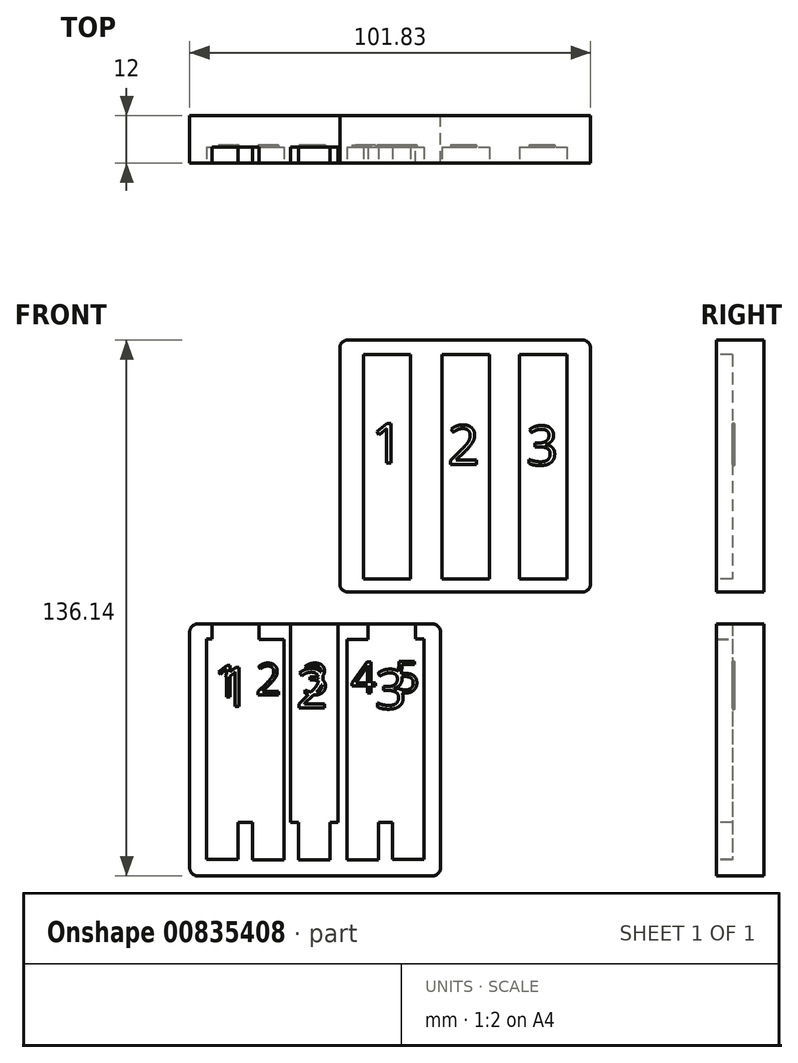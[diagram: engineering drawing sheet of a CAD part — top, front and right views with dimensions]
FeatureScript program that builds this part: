
annotation { "Feature Type Name" : "Feature", "Feature Type Description" : "" }
export const myFeature = defineFeature(function(context is Context, id is Id, definition is map)
    precondition{}
    {
        {
            var Q0;
            Q0=qCreatedBy(makeId("Front.planeOp"),FACE);
            var sketch = newSketch(context, id + "F0", { "sketchPlane" : qUnion([Q0])});
            skLineSegment(sketch, "E0.bottom", {"start": v(-35.21, 33.45) * mm, "end": v(28.49, 33.45) * mm});
            skLineSegment(sketch, "E0.top", {"start": v(-35.21, -30.55) * mm, "end": v(28.49, -30.55) * mm});
            skLineSegment(sketch, "E0.left", {"start": v(-35.21, 33.45) * mm, "end": v(-35.21, -30.55) * mm});
            skLineSegment(sketch, "E0.right", {"start": v(28.49, 33.45) * mm, "end": v(28.49, -30.55) * mm});
            skSolve(sketch);
        }
        {
            var Q0;
            Q0 = qSketchRegion(id + "F0", true);
            extrude(context, id + "F1", {"entities" : qUnion([Q0]), "depth" : 12 * mm, "offsetDistance" : 25 * mm});
        }
        {
            var Q0;
            Q0=makeQuery(id+"F1.opExtrude","CAP_FACE",FACE,{"disambiguationData":[OSD([sQuery(id+"F0.wireOp",EDGE,"E0.bottom"),sQuery(id+"F0.wireOp",EDGE,"E0.top"),sQuery(id+"F0.wireOp",EDGE,"E0.left"),sQuery(id+"F0.wireOp",EDGE,"E0.right")])],"isStart":false});
            var sketch = newSketch(context, id + "F2", { "sketchPlane" : qUnion([Q0])});
            skLineSegment(sketch, "E1.bottom", {"start": v(-30.9, 29.6) * mm, "end": v(-22.9, 29.6) * mm});
            skLineSegment(sketch, "E1.top", {"start": v(-30.9, -26.4) * mm, "end": v(-22.9, -26.4) * mm});
            skLineSegment(sketch, "E1.left", {"start": v(-30.9, 29.6) * mm, "end": v(-30.9, -26.4) * mm});
            skLineSegment(sketch, "E1.right", {"start": v(-22.9, 29.6) * mm, "end": v(-22.9, -26.4) * mm});
            skLineSegment(sketch, "E2.bottom", {"start": v(-19.28, 29.54) * mm, "end": v(-11.28, 29.54) * mm});
            skLineSegment(sketch, "E2.top", {"start": v(-19.28, -26.46) * mm, "end": v(-11.28, -26.46) * mm});
            skLineSegment(sketch, "E2.left", {"start": v(-19.28, 29.54) * mm, "end": v(-19.28, -26.46) * mm});
            skLineSegment(sketch, "E2.right", {"start": v(-11.28, 29.54) * mm, "end": v(-11.28, -26.46) * mm});
            skLineSegment(sketch, "E3.bottom", {"start": v(-7.55, 29.54) * mm, "end": v(0.45, 29.54) * mm});
            skLineSegment(sketch, "E3.top", {"start": v(-7.55, -26.46) * mm, "end": v(0.45, -26.46) * mm});
            skLineSegment(sketch, "E3.left", {"start": v(-7.55, 29.54) * mm, "end": v(-7.55, -26.46) * mm});
            skLineSegment(sketch, "E3.right", {"start": v(0.45, 29.54) * mm, "end": v(0.45, -26.46) * mm});
            skLineSegment(sketch, "E4.bottom", {"start": v(4.75, 29.54) * mm, "end": v(12.75, 29.54) * mm});
            skLineSegment(sketch, "E4.top", {"start": v(4.75, -26.46) * mm, "end": v(12.75, -26.46) * mm});
            skLineSegment(sketch, "E4.left", {"start": v(4.75, 29.54) * mm, "end": v(4.75, -26.46) * mm});
            skLineSegment(sketch, "E4.right", {"start": v(12.75, 29.54) * mm, "end": v(12.75, -26.46) * mm});
            skLineSegment(sketch, "E5.bottom", {"start": v(16.3, 29.59) * mm, "end": v(24.3, 29.59) * mm});
            skLineSegment(sketch, "E5.top", {"start": v(16.3, -26.41) * mm, "end": v(24.3, -26.41) * mm});
            skLineSegment(sketch, "E5.left", {"start": v(16.3, 29.59) * mm, "end": v(16.3, -26.41) * mm});
            skLineSegment(sketch, "E5.right", {"start": v(24.3, 29.59) * mm, "end": v(24.3, -26.41) * mm});
            skSolve(sketch);
        }
        {
            var Q0;
            Q0 = qSketchRegion(id + "F2", true);
            extrude(context, id + "F3", {"entities" : qUnion([Q0]), "operationType" : NewBodyOperationType.REMOVE, "oppositeDirection" : true, "depth" : 4 * mm, "offsetDistance" : 25 * mm});
        }
        {
            var Q0;
            Q0=makeQuery(id+"F3.boolean.opBoolean","COPY",FACE,{"derivedFrom":makeQuery(id+"F3.opExtrude","CAP_FACE",FACE,{"disambiguationData":[OSD([sQuery(id+"F2.wireOp",EDGE,"E1.bottom"),sQuery(id+"F2.wireOp",EDGE,"E1.top"),sQuery(id+"F2.wireOp",EDGE,"E1.left"),sQuery(id+"F2.wireOp",EDGE,"E1.right")])],"isStart":false})});
            var sketch = newSketch(context, id + "F4", { "sketchPlane" : qUnion([Q0])});
            skText(sketch, "E6", { "text": "1", "fontName": "OpenSans-Regular.ttf"});
            skText(sketch, "E7", { "text": "2", "fontName": "OpenSans-Regular.ttf"});
            skText(sketch, "E8", { "text": "3", "fontName": "OpenSans-Regular.ttf"});
            skText(sketch, "E9", { "text": "4", "fontName": "OpenSans-Regular.ttf"});
            skText(sketch, "E10", { "text": "5", "fontName": "OpenSans-Regular.ttf"});
            const initialGuessF4  = {"E6": [-0.0289, 0.01496, 1, 0, 0.008], "E7": [-0.01839, 0.01547, 1, 0, 0.008], "E8": [-0.00642, 0.01547, 1, 0, 0.008], "E9": [0.00585, 0.01587, 1, 0, 0.008], "E10": [0.01678, 0.01602, 1, 0, 0.008]};
            skSetInitialGuess(sketch, initialGuessF4);
            skSolve(sketch);
        }
        {
            var Q0;
            Q0 = qSketchRegion(id + "F4", true);
            extrude(context, id + "F5", {"entities" : qUnion([Q0]), "operationType" : NewBodyOperationType.REMOVE, "oppositeDirection" : true, "depth" : 0.5 * mm, "offsetDistance" : 25 * mm});
        }
        {
            var Q0;
            Q0=qCreatedBy(makeId("Front.planeOp"),FACE);
            var sketch = newSketch(context, id + "F6", { "sketchPlane" : qUnion([Q0])});
            skLineSegment(sketch, "E11.bottom", {"start": v(-35.58, 43.69) * mm, "end": v(28.12, 43.69) * mm});
            skLineSegment(sketch, "E11.top", {"start": v(-35.58, -20.31) * mm, "end": v(28.12, -20.31) * mm});
            skLineSegment(sketch, "E11.left", {"start": v(-35.58, 43.69) * mm, "end": v(-35.58, -20.31) * mm});
            skLineSegment(sketch, "E11.right", {"start": v(28.12, 43.69) * mm, "end": v(28.12, -20.31) * mm});
            skSolve(sketch);
        }
        {
            var Q0;
            Q0=makeQuery(id+"F6.imprint","IMPRINT",FACE,{"disambiguationData":[TD([[makeQuery(id+"F6.imprint","IMPRINT",EDGE,{"derivedFrom":sQuery(id+"F6.wireOp",EDGE,"E11.bottom")}),-1.0]])]});
            extrude(context, id + "F7", {"entities" : qUnion([Q0]), "depth" : 12 * mm, "offsetDistance" : 25 * mm});
        }
        {
            var Q0;
            Q0=makeQuery(id+"F7.opExtrude","CAP_FACE",FACE,{"disambiguationData":[OSD([sQuery(id+"F6.wireOp",EDGE,"E11.bottom"),sQuery(id+"F6.wireOp",EDGE,"E11.top"),sQuery(id+"F6.wireOp",EDGE,"E11.left"),sQuery(id+"F6.wireOp",EDGE,"E11.right")])],"isStart":false});
            var sketch = newSketch(context, id + "F8", { "sketchPlane" : qUnion([Q0])});
            skLineSegment(sketch, "E12.bottom", {"start": v(-29.58, 40.02) * mm, "end": v(-17.58, 40.02) * mm});
            skLineSegment(sketch, "E12.top", {"start": v(-29.58, -16.98) * mm, "end": v(-17.58, -16.98) * mm});
            skLineSegment(sketch, "E12.left", {"start": v(-29.58, 40.02) * mm, "end": v(-29.58, -16.98) * mm});
            skLineSegment(sketch, "E12.right", {"start": v(-17.58, 40.02) * mm, "end": v(-17.58, -16.98) * mm});
            skLineSegment(sketch, "E13.bottom", {"start": v(-9.58, 40.02) * mm, "end": v(2.42, 40.02) * mm});
            skLineSegment(sketch, "E13.top", {"start": v(-9.58, -16.98) * mm, "end": v(2.42, -16.98) * mm});
            skLineSegment(sketch, "E13.left", {"start": v(-9.58, 40.02) * mm, "end": v(-9.58, -16.98) * mm});
            skLineSegment(sketch, "E13.right", {"start": v(2.42, 40.02) * mm, "end": v(2.42, -16.98) * mm});
            skLineSegment(sketch, "E14.bottom", {"start": v(10.12, 40.02) * mm, "end": v(22.12, 40.02) * mm});
            skLineSegment(sketch, "E14.top", {"start": v(10.12, -16.98) * mm, "end": v(22.12, -16.98) * mm});
            skLineSegment(sketch, "E14.left", {"start": v(10.12, 40.02) * mm, "end": v(10.12, -16.98) * mm});
            skLineSegment(sketch, "E14.right", {"start": v(22.12, 40.02) * mm, "end": v(22.12, -16.98) * mm});
            skSolve(sketch);
        }
        {
            var Q0;
            Q0 = qSketchRegion(id + "F8", true);
            extrude(context, id + "F9", {"entities" : qUnion([Q0]), "operationType" : NewBodyOperationType.REMOVE, "oppositeDirection" : true, "depth" : 4 * mm, "offsetDistance" : 25 * mm});
        }
        {
            var Q0;
            Q0=makeQuery(id+"F9.boolean.opBoolean","COPY",FACE,{"derivedFrom":makeQuery(id+"F9.opExtrude","CAP_FACE",FACE,{"disambiguationData":[OSD([sQuery(id+"F8.wireOp",EDGE,"E12.bottom"),sQuery(id+"F8.wireOp",EDGE,"E12.top"),sQuery(id+"F8.wireOp",EDGE,"E12.left"),sQuery(id+"F8.wireOp",EDGE,"E12.right")])],"isStart":false})});
            var sketch = newSketch(context, id + "F10", { "sketchPlane" : qUnion([Q0])});
            skText(sketch, "E15", { "text": "1", "fontName": "OpenSans-Regular.ttf"});
            skText(sketch, "E16", { "text": "2", "fontName": "OpenSans-Regular.ttf"});
            skText(sketch, "E17", { "text": "3", "fontName": "OpenSans-Regular.ttf"});
            const initialGuessF10  = {"E15": [-0.02746, 0.0125, 1, 0, 0.01], "E16": [-0.0081, 0.0121, 1, 0, 0.01], "E17": [0.0119, 0.01192, 1, 0, 0.01]};
            skSetInitialGuess(sketch, initialGuessF10);
            skSolve(sketch);
        }
        {
            var Q0;
            Q0 = qSketchRegion(id + "F10", true);
            extrude(context, id + "F11", {"entities" : qUnion([Q0]), "operationType" : NewBodyOperationType.REMOVE, "oppositeDirection" : true, "depth" : 0.5 * mm, "offsetDistance" : 25 * mm});
        }
        {
            var Q0;
            Q0=makeQuery(id+"F7.opExtrude","SWEPT_EDGE",EDGE,{"disambiguationData":[OSD([sQuery(id+"F6.wireOp",EDGE,"E11.top"),sQuery(id+"F6.wireOp",EDGE,"E11.left")])]});
            var Q1;
            Q1=makeQuery(id+"F7.opExtrude","SWEPT_EDGE",EDGE,{"disambiguationData":[OSD([sQuery(id+"F6.wireOp",EDGE,"E11.top"),sQuery(id+"F6.wireOp",EDGE,"E11.right")])]});
            var Q2;
            Q2=makeQuery(id+"F7.opExtrude","SWEPT_EDGE",EDGE,{"disambiguationData":[OSD([sQuery(id+"F6.wireOp",EDGE,"E11.bottom"),sQuery(id+"F6.wireOp",EDGE,"E11.right")])]});
            var Q3;
            Q3=makeQuery(id+"F7.opExtrude","SWEPT_EDGE",EDGE,{"disambiguationData":[OSD([sQuery(id+"F6.wireOp",EDGE,"E11.bottom"),sQuery(id+"F6.wireOp",EDGE,"E11.left")])]});
            fillet(context, id + "F12", {"entities" : qUnion([Q0, Q1, Q2, Q3]), "radius" : 2 * mm, "tangentPropagation" : true, "allowEdgeOverflow" : false});
        }
        {
            var Q0;
            Q0=makeQuery(id+"F7.opExtrude","SWEPT_BODY",BODY,{"disambiguationData":[OSD([sQuery(id+"F6.wireOp",EDGE,"E11.bottom"),sQuery(id+"F6.wireOp",EDGE,"E11.top"),sQuery(id+"F6.wireOp",EDGE,"E11.left"),sQuery(id+"F6.wireOp",EDGE,"E11.right")])]});
            transform(context, id + "F13", {"entities" : qUnion([Q0]), "transformType" : TransformType.TRANSLATION_3D, "dx" : 38.5 * mm, "dy" : 0 * mm, "dz" : 40.6 * mm, "makeCopy" : false});
        }
        {
            var Q0;
            Q0=makeQuery(id+"F1.opExtrude","SWEPT_BODY",BODY,{"disambiguationData":[OSD([sQuery(id+"F0.wireOp",EDGE,"E0.bottom"),sQuery(id+"F0.wireOp",EDGE,"E0.top"),sQuery(id+"F0.wireOp",EDGE,"E0.left"),sQuery(id+"F0.wireOp",EDGE,"E0.right")])]});
            transform(context, id + "F14", {"entities" : qUnion([Q0]), "transformType" : TransformType.TRANSLATION_3D, "dx" : 0 * mm, "dy" : 0 * mm, "dz" : -21.3 * mm, "makeCopy" : false});
        }
        {
            var Q0;
            Q0=makeQuery(id+"F1.opExtrude","SWEPT_EDGE",EDGE,{"disambiguationData":[OSD([sQuery(id+"F0.wireOp",EDGE,"E0.top"),sQuery(id+"F0.wireOp",EDGE,"E0.left")])]});
            var Q1;
            Q1=makeQuery(id+"F1.opExtrude","SWEPT_EDGE",EDGE,{"disambiguationData":[OSD([sQuery(id+"F0.wireOp",EDGE,"E0.top"),sQuery(id+"F0.wireOp",EDGE,"E0.right")])]});
            var Q2;
            Q2=makeQuery(id+"F1.opExtrude","SWEPT_EDGE",EDGE,{"disambiguationData":[OSD([sQuery(id+"F0.wireOp",EDGE,"E0.bottom"),sQuery(id+"F0.wireOp",EDGE,"E0.left")])]});
            var Q3;
            Q3=makeQuery(id+"F1.opExtrude","SWEPT_EDGE",EDGE,{"disambiguationData":[OSD([sQuery(id+"F0.wireOp",EDGE,"E0.bottom"),sQuery(id+"F0.wireOp",EDGE,"E0.right")])]});
            fillet(context, id + "F15", {"entities" : qUnion([Q0, Q1, Q2, Q3]), "radius" : 2 * mm, "tangentPropagation" : true, "allowEdgeOverflow" : false});
        }
    });
